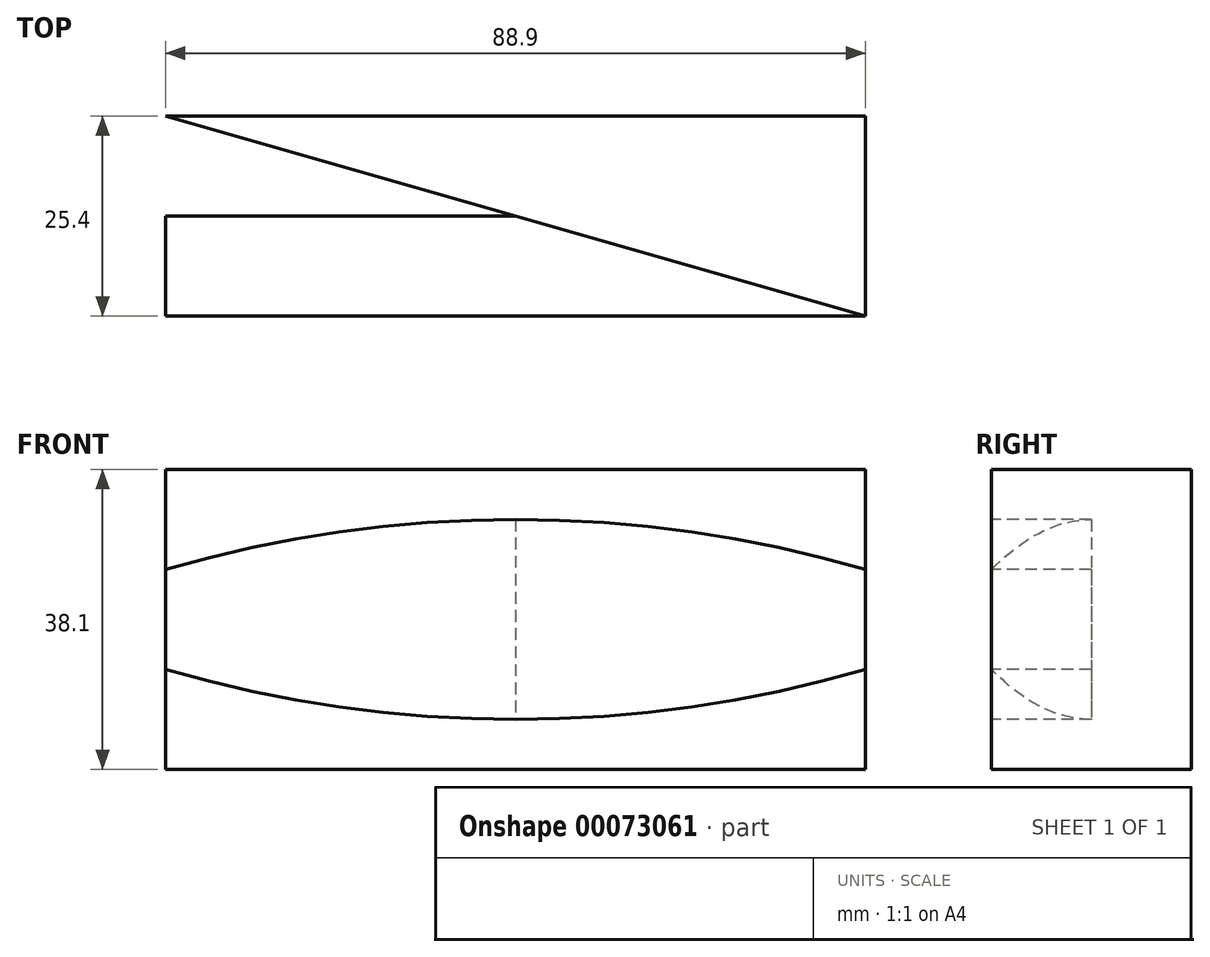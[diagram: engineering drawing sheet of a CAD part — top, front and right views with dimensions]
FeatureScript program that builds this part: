
annotation { "Feature Type Name" : "Feature", "Feature Type Description" : "" }
export const myFeature = defineFeature(function(context is Context, id is Id, definition is map)
    precondition{}
    {
        {
            var Q0;
            Q0=qCreatedBy(makeId("Front.planeOp"),FACE);
            var sketch = newSketch(context, id + "F0", { "sketchPlane" : qUnion([Q0])});
            skLineSegment(sketch, "E0.rect.bottom", {"start": v(44.45, 19.05) * mm, "end": v(-44.45, 19.05) * mm});
            skLineSegment(sketch, "E0.rect.top", {"start": v(44.45, -19.05) * mm, "end": v(-44.45, -19.05) * mm});
            skLineSegment(sketch, "E0.rect.left", {"start": v(44.45, 19.05) * mm, "end": v(44.45, -19.05) * mm});
            skLineSegment(sketch, "E0.rect.right", {"start": v(-44.45, 19.05) * mm, "end": v(-44.45, -19.05) * mm});
            skPoint(sketch, "E0.rect.middle", {"position": v(0, 0) * mm});
            skSolve(sketch);
        }
        {
            var Q0;
            Q0=makeQuery(id+"F0.imprint","IMPRINT",FACE,{"disambiguationData":[TD([[makeQuery(id+"F0.imprint","IMPRINT",EDGE,{"derivedFrom":sQuery(id+"F0.wireOp",EDGE,"E0.rect.bottom")}),1.0]])]});
            extrude(context, id + "F1", {"entities" : qUnion([Q0]), "oppositeDirection" : true, "depth" : 25.4 * mm});
        }
        {
            var Q0;
            Q0=qCreatedBy(makeId("Front.planeOp"),FACE);
            var sketch = newSketch(context, id + "F2", { "sketchPlane" : qUnion([Q0])});
            skArc(sketch, "E1", {"start": v(44.45, 6.35) * mm, "mid": v(0, 12.7) * mm, "end": v(-44.45, 6.35) * mm});
            skArc(sketch, "E2", {"start": v(-44.45, -6.35) * mm, "mid": v(0, -12.7) * mm, "end": v(44.45, -6.35) * mm});
            skLineSegment(sketch, "E3.0", {"start": v(-44.45, 6.35) * mm, "end": v(-44.45, -6.35) * mm});
            skLineSegment(sketch, "E4.0", {"start": v(44.45, 6.35) * mm, "end": v(44.45, -6.35) * mm});
            skPoint(sketch, "E5.orphan", {"position": v(44.45, 19.05) * mm});
            skPoint(sketch, "E6.orphan", {"position": v(44.45, -19.05) * mm});
            skPoint(sketch, "E7.orphan", {"position": v(-44.45, -19.05) * mm});
            skPoint(sketch, "E8.orphan", {"position": v(-44.45, 19.05) * mm});
            skSolve(sketch);
        }
        {
            var Q0;
            Q0 = qSketchRegion(id + "F2", true);
            extrude(context, id + "F3", {"entities" : qUnion([Q0]), "operationType" : NewBodyOperationType.REMOVE, "oppositeDirection" : true, "depth" : 12.7 * mm});
        }
        {
            var Q0;
            Q0=qCreatedBy(makeId("Top.planeOp"),FACE);
            var sketch = newSketch(context, id + "F4", { "sketchPlane" : qUnion([Q0])});
            skLineSegment(sketch, "E9.0", {"start": v(44.45, 0) * mm, "end": v(-44.45, 0) * mm});
            skLineSegment(sketch, "E10.0", {"start": v(-44.45, 25.4) * mm, "end": v(-44.45, 0) * mm});
            skLineSegment(sketch, "E11", {"start": v(-44.45, 25.4) * mm, "end": v(44.45, 0) * mm});
            skSolve(sketch);
        }
        {
            var Q0;
            Q0=makeQuery(id+"F4.imprint","IMPRINT",FACE,{"disambiguationData":[TD([[makeQuery(id+"F4.imprint","IMPRINT",EDGE,{"derivedFrom":sQuery(id+"F4.wireOp",EDGE,"E9.0")}),-1.0]])]});
            extrude(context, id + "F5", {"entities" : qUnion([Q0]), "operationType" : NewBodyOperationType.REMOVE, "oppositeDirection" : true, "depth" : 25.4 * mm, "hasSecondDirection" : true, "secondDirectionOppositeDirection" : false, "secondDirectionDepth" : 25.4 * mm});
        }
        {
            var Q0;
            Q0=makeQuery(id+"F1.opExtrude","SWEPT_FACE",FACE,{"disambiguationData":[OSD([sQuery(id+"F0.wireOp",EDGE,"E0.rect.left")])]});
            var sketch = newSketch(context, id + "F6", { "sketchPlane" : qUnion([Q0])});
            skLineSegment(sketch, "E12.0", {"start": v(12.7, 12.7) * mm, "end": v(12.7, 6.35) * mm});
            skLineSegment(sketch, "E13.0", {"start": v(12.7, 6.35) * mm, "end": v(0, 6.35) * mm});
            skLineSegment(sketch, "E14.0", {"start": v(12.7, -6.35) * mm, "end": v(0, -6.35) * mm});
            skLineSegment(sketch, "E15", {"start": v(12.7, 12.7) * mm, "end": v(0, 6.35) * mm});
            skLineSegment(sketch, "E16", {"start": v(12.7, -12.7) * mm, "end": v(0, -6.35) * mm});
            skLineSegment(sketch, "E17.trimOffspring", {"start": v(12.7, -6.35) * mm, "end": v(12.7, -12.7) * mm});
            skSolve(sketch);
        }
        {
            var Q0;
            Q0 = qSketchRegion(id + "F6", true);
            extrude(context, id + "F7", {"entities" : qUnion([Q0]), "operationType" : NewBodyOperationType.REMOVE, "oppositeDirection" : true, "depth" : 50.8 * mm});
        }
        {
            var Q0;
            Q0=makeQuery(id+"F1.opExtrude","SWEPT_FACE",FACE,{"disambiguationData":[OSD([sQuery(id+"F0.wireOp",EDGE,"E0.rect.left")])]});
            var sketch = newSketch(context, id + "F8", { "sketchPlane" : qUnion([Q0])});
            skLineSegment(sketch, "E18.0", {"start": v(12.7, 12.7) * mm, "end": v(0, 6.35) * mm});
            skLineSegment(sketch, "E19.0", {"start": v(12.7, 12.7) * mm, "end": v(12.7, -12.7) * mm});
            skLineSegment(sketch, "E20.0", {"start": v(12.7, -12.7) * mm, "end": v(0, -6.35) * mm});
            skLineSegment(sketch, "E21", {"start": v(0, -6.35) * mm, "end": v(0, 6.35) * mm});
            skSolve(sketch);
        }
        {
            var Q0;
            Q0=makeQuery(id+"F8.imprint","IMPRINT",FACE,{"disambiguationData":[TD([[makeQuery(id+"F8.imprint","IMPRINT",EDGE,{"derivedFrom":sQuery(id+"F8.wireOp",EDGE,"E18.0")}),1.0]])]});
            extrude(context, id + "F9", {"entities" : qUnion([Q0]), "oppositeDirection" : true, "depth" : 44.45 * mm});
        }
        {
            var Q0;
            Q0 = qSketchRegion(id + "F2", true);
            extrude(context, id + "F10", {"entities" : qUnion([Q0]), "operationType" : NewBodyOperationType.ADD, "oppositeDirection" : true, "depth" : 12.7 * mm});
        }
    });
